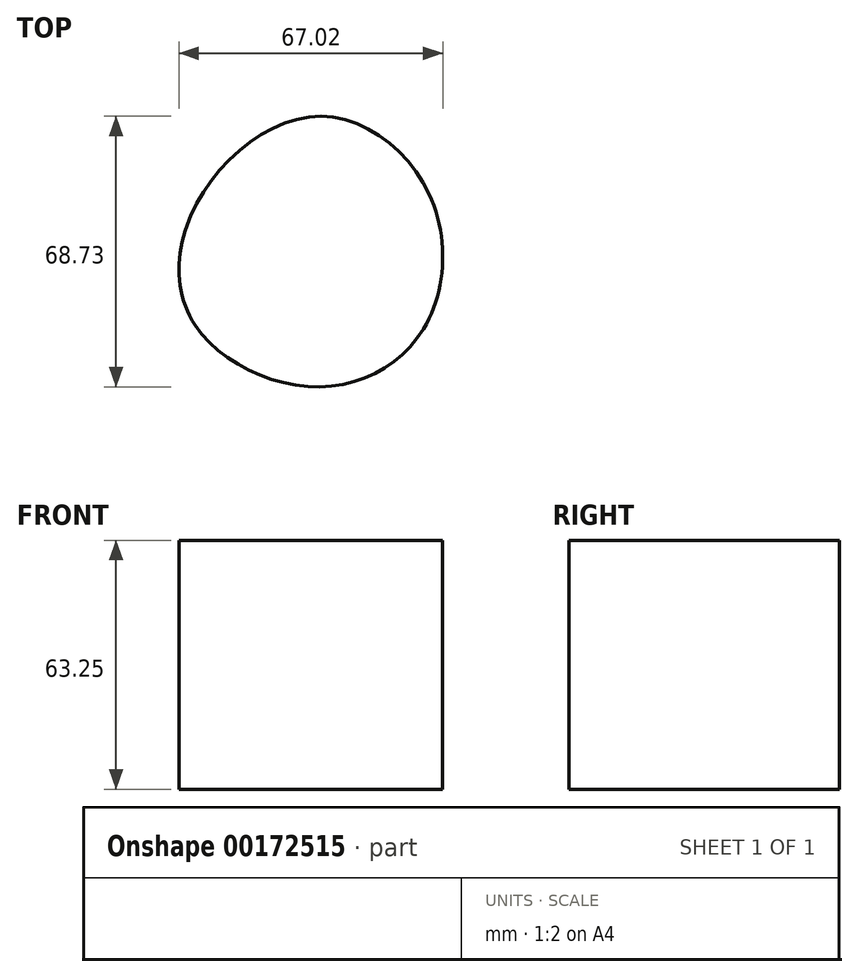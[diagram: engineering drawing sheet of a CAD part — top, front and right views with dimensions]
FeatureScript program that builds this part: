
annotation { "Feature Type Name" : "Feature", "Feature Type Description" : "" }
export const myFeature = defineFeature(function(context is Context, id is Id, definition is map)
    precondition{}
    {
        {
            var Q0;
            Q0=qCreatedBy(makeId("Top.planeOp"),FACE);
            var sketch = newSketch(context, id + "F0", { "sketchPlane" : qUnion([Q0])});
            skFitSpline(sketch, "E0", {"points": [v(-31.04, 14.3) * mm, v(0, 36.48) * mm, v(28.01, 16.73) * mm, v(26.6, -17.53) * mm, v(0, -32.25) * mm, v(-31.44, -16.53) * mm, v(-31.04, 14.3) * mm]});
            skFitSpline(sketch, "E1", {"points": [v(-31.04, 14.3) * mm, v(0, 0) * mm, v(28.01, 16.73) * mm], "startDerivative": vector(62.54, -44) * mm, "endDerivative": vector(55.53, 49.2) * mm});
            skFitSpline(sketch, "E2", {"points": [v(0, 0) * mm, v(26.6, -17.53) * mm], "startDerivative": vector(26.6, -17.53) * mm, "endDerivative": vector(26.6, -17.53) * mm});
            skFitSpline(sketch, "E3", {"points": [v(0, 0) * mm, v(-31.44, -16.53) * mm], "startDerivative": vector(-31.44, -16.53) * mm, "endDerivative": vector(-31.44, -16.53) * mm});
            skSolve(sketch);
        }
        {
            var Q0;
            {var subQ0=sQuery(id+"F0.wireOp",EDGE,"E1");var subQ1=sQuery(id+"F0.wireOp",EDGE,"E0");var subQ2=makeQuery(id+"F0.imprint","INTERSECT",VERTEX,{"disambiguationData":[OD(0.0)],"derivedFrom":[subQ1,subQ0]});Q0=makeQuery(id+"F0.imprint","IMPRINT",FACE,{"disambiguationData":[TD([[makeQuery(id+"F0.imprint","IMPRINT",EDGE,{"disambiguationData":[TD([[subQ2,-1.0]])],"derivedFrom":subQ1}),-1.0]])]});}
            var Q1;
            {var subQ0=sQuery(id+"F0.wireOp",EDGE,"E2");Q1=makeQuery(id+"F0.imprint","IMPRINT",FACE,{"disambiguationData":[TD([[makeQuery(id+"F0.imprint","IMPRINT",EDGE,{"derivedFrom":subQ0}),-1.0]])]});}
            var Q2;
            {var subQ3=sQuery(id+"F0.wireOp",EDGE,"E2");Q2=makeQuery(id+"F0.imprint","IMPRINT",FACE,{"disambiguationData":[TD([[makeQuery(id+"F0.imprint","IMPRINT",EDGE,{"derivedFrom":subQ3}),1.0]])]});}
            var Q3;
            {var subQ3=sQuery(id+"F0.wireOp",EDGE,"E3");Q3=makeQuery(id+"F0.imprint","IMPRINT",FACE,{"disambiguationData":[TD([[makeQuery(id+"F0.imprint","IMPRINT",EDGE,{"derivedFrom":subQ3}),-1.0]])]});}
            extrude(context, id + "F1", {"entities" : qUnion([Q0, Q1, Q2, Q3]), "depth" : 63.25 * mm});
        }
    });
